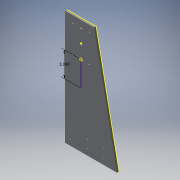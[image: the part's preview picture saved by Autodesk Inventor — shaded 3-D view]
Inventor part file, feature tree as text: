
AUTODESK INVENTOR PART (.ipt)
format: ipt  version: 2016 (Build 200138000, 138)  size: 171,008 bytes
history: native  units: in
note: dims shown in document units (in); Inventor stores cm internally (conversion verified against a paired STEP export)
features: sketch x6, extrude x4, reference x2, projected_geometry x2, plane x1
ambient origin geometry x8: Origin, YZ Plane, XZ Plane, XY Plane, X Axis, Y Axis, Z Axis, Center Point
bodies: Solid1 (feature_tree)
feature tree (15):
  plane  "Work Plane1"
  extrude  "Extrusion1"  Depth=0.5in
  extrude  "Extrusion2"  Depth=0.24in TaperAngle=0.0deg
  extrude  "Extrusion3"  Depth=13.75in
  sketch  "Sketch4"  dims[d11=0.5in d12=1.0in]
  sketch  "Sketch5"  dims[d13=0.175in]
  extrude  "Extrusion4"  Depth=1.0in
  sketch  "Sketch1"  dims[d0=0.414in d1=0.5in]
  reference  "Reference1"
  sketch  "Sketch2"  dims[d4=3.5in d6=0.24in d7=0.0in]
  reference  "Reference2"
  sketch  "Sketch3"  dims[d8=1.0in d9=0.0in d10=13.75in]
  projected_geometry  "Projected Loop1"
  projected_geometry  "Projected Loop2"
  sketch  "Sketch6"  dims[d14=0.175in d15=0.175in d16=0.175in d17=0.175in d18=0.175in d19=1.0in d20=0.0in d21=3.0in d22=6.0in d23=0.5in d24=1.5in d25=0.175in d26=0.175in d27=1.0in d28=0.0in]
